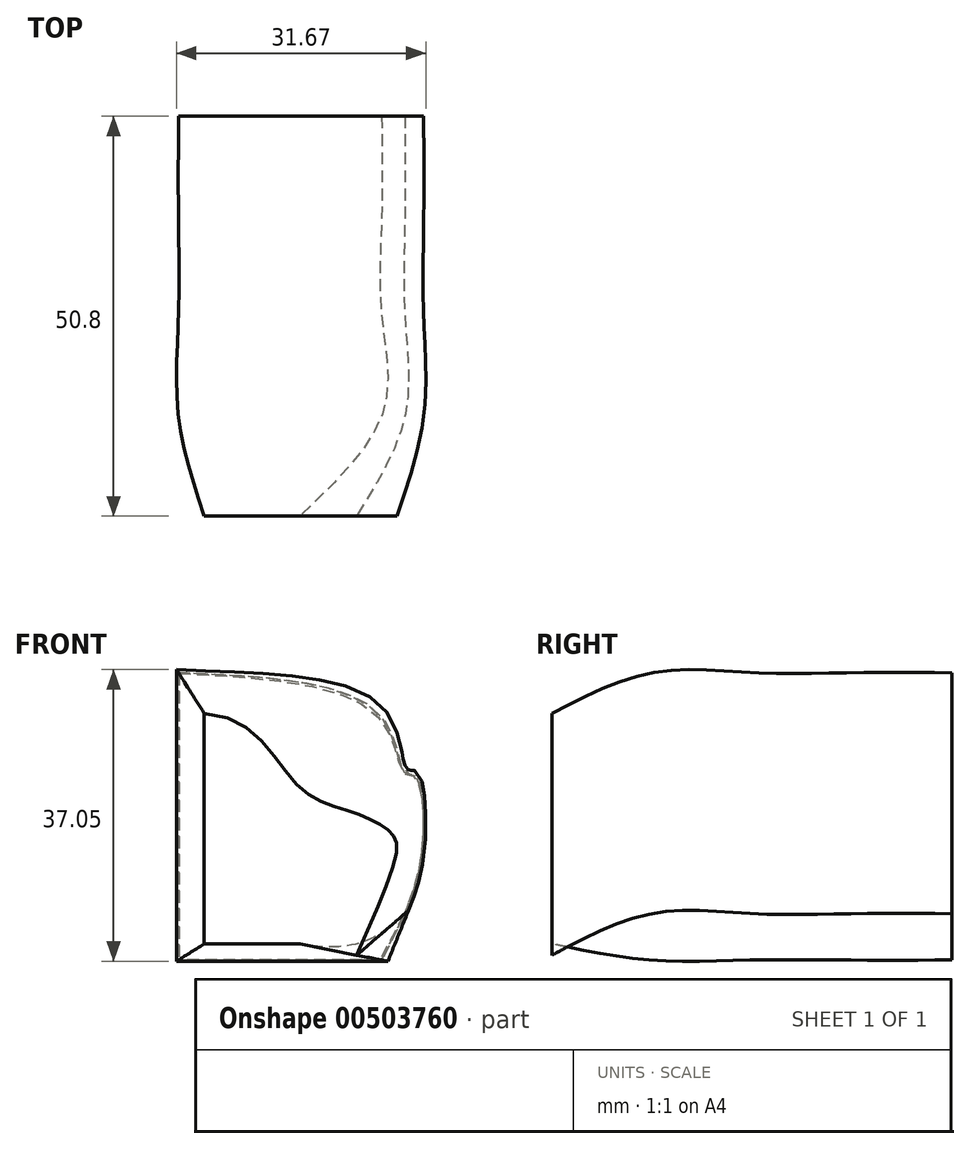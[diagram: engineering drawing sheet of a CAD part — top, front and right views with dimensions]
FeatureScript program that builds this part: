
annotation { "Feature Type Name" : "Feature", "Feature Type Description" : "" }
export const myFeature = defineFeature(function(context is Context, id is Id, definition is map)
    precondition{}
    {
        {
            var Q0;
            Q0=qCreatedBy(makeId("Front.planeOp"),FACE);
            cPlane(context, id + "F0", {"entities" : qUnion([Q0]), "cplaneType" : CPlaneType.OFFSET, "offset" : 25.4 * mm, "width" : 152.4 * mm, "height" : 152.4 * mm});
        }
        {
            var Q0;
            Q0=qCreatedBy(id+"F0.planeOp",FACE);
            cPlane(context, id + "F1", {"entities" : qUnion([Q0]), "cplaneType" : CPlaneType.OFFSET, "offset" : 12.7 * mm, "width" : 152.4 * mm, "height" : 152.4 * mm});
        }
        {
            var Q0;
            Q0=qCreatedBy(id+"F1.planeOp",FACE);
            cPlane(context, id + "F2", {"entities" : qUnion([Q0]), "cplaneType" : CPlaneType.OFFSET, "offset" : 12.7 * mm, "width" : 152.4 * mm, "height" : 152.4 * mm});
        }
        {
            var Q0;
            Q0=qCreatedBy(id+"F0.planeOp",FACE);
            cPlane(context, id + "F3", {"entities" : qUnion([Q0]), "cplaneType" : CPlaneType.OFFSET, "offset" : 12.7 * mm, "oppositeDirection" : true, "width" : 152.4 * mm, "height" : 152.4 * mm});
        }
        {
            var Q0;
            Q0=qCreatedBy(id+"F3.planeOp",FACE);
            cPlane(context, id + "F4", {"entities" : qUnion([Q0]), "cplaneType" : CPlaneType.OFFSET, "offset" : 12.7 * mm, "oppositeDirection" : true, "width" : 152.4 * mm, "height" : 152.4 * mm});
        }
        {
            var Q0;
            Q0=qCreatedBy(id+"F1.planeOp",FACE);
            var sketch = newSketch(context, id + "F5", { "sketchPlane" : qUnion([Q0])});
            skLineSegment(sketch, "E0", {"start": v(-15.42, -12) * mm, "end": v(10.4, -12) * mm});
            skLineSegment(sketch, "E1", {"start": v(10.4, -12) * mm, "end": v(13.34, -6.1) * mm});
            skFitSpline(sketch, "E2", {"points": [v(13.34, -6.1) * mm, v(15.55, 2) * mm, v(14.63, 11.4) * mm, v(13.34, 11.77) * mm, v(10.4, 18.78) * mm, v(-15.42, 24.5) * mm], "startDerivative": vector(14.36, 36.3) * mm, "endDerivative": vector(-96.3, 4.27) * mm});
            skLineSegment(sketch, "E3", {"start": v(-15.42, 24.5) * mm, "end": v(-15.42, -12) * mm});
            skSolve(sketch);
        }
        {
            var Q0;
            Q0=qCreatedBy(id+"F0.planeOp",FACE);
            var sketch = newSketch(context, id + "F6", { "sketchPlane" : qUnion([Q0])});
            skLineSegment(sketch, "E4", {"start": v(-15.42, -12) * mm, "end": v(10.4, -12) * mm});
            skLineSegment(sketch, "E5", {"start": v(10.4, -12) * mm, "end": v(13.34, -6.1) * mm});
            skFitSpline(sketch, "E6", {"points": [v(13.34, -6.1) * mm, v(15.55, 2) * mm, v(14.63, 11.4) * mm, v(13.34, 11.77) * mm, v(10.4, 18.78) * mm, v(-15.42, 24.5) * mm], "startDerivative": vector(14.36, 36.3) * mm, "endDerivative": vector(-96.3, 4.27) * mm});
            skLineSegment(sketch, "E7", {"start": v(-15.42, 24.5) * mm, "end": v(-15.42, -12) * mm});
            skSolve(sketch);
        }
        {
            var Q0;
            Q0=qCreatedBy(id+"F3.planeOp",FACE);
            var sketch = newSketch(context, id + "F7", { "sketchPlane" : qUnion([Q0])});
            skLineSegment(sketch, "E8", {"start": v(-15.42, -12) * mm, "end": v(10.4, -12) * mm});
            skLineSegment(sketch, "E9", {"start": v(10.4, -12) * mm, "end": v(13.34, -6.1) * mm});
            skFitSpline(sketch, "E10", {"points": [v(13.34, -6.1) * mm, v(15.55, 2) * mm, v(14.63, 11.4) * mm, v(13.34, 11.77) * mm, v(10.4, 18.78) * mm, v(-15.42, 24.5) * mm], "startDerivative": vector(14.36, 36.3) * mm, "endDerivative": vector(-96.3, 4.27) * mm});
            skLineSegment(sketch, "E11", {"start": v(-15.42, 24.5) * mm, "end": v(-15.42, -12) * mm});
            skSolve(sketch);
        }
        {
            var Q0;
            Q0=qCreatedBy(id+"F4.planeOp",FACE);
            var sketch = newSketch(context, id + "F8", { "sketchPlane" : qUnion([Q0])});
            skLineSegment(sketch, "E12", {"start": v(-15.42, -12) * mm, "end": v(10.4, -12) * mm});
            skLineSegment(sketch, "E13", {"start": v(10.4, -12) * mm, "end": v(13.34, -6.1) * mm});
            skFitSpline(sketch, "E14", {"points": [v(13.34, -6.1) * mm, v(15.55, 2) * mm, v(14.63, 11.4) * mm, v(13.34, 11.77) * mm, v(10.4, 18.78) * mm, v(-15.42, 24.5) * mm], "startDerivative": vector(14.36, 36.3) * mm, "endDerivative": vector(-96.3, 4.27) * mm});
            skLineSegment(sketch, "E15", {"start": v(-15.42, 24.5) * mm, "end": v(-15.42, -12) * mm});
            skSolve(sketch);
        }
        {
            var Q0;
            Q0=qCreatedBy(id+"F2.planeOp",FACE);
            var sketch = newSketch(context, id + "F9", { "sketchPlane" : qUnion([Q0])});
            skLineSegment(sketch, "E16", {"start": v(-12.15, -9.94) * mm, "end": v(0, -9.94) * mm});
            skLineSegment(sketch, "E17", {"start": v(7.21, -11.4) * mm, "end": v(0, -9.94) * mm});
            skFitSpline(sketch, "E18", {"points": [v(7.21, -11.4) * mm, v(12.25, 1.58) * mm, v(11.44, 4.28) * mm, v(7.21, 6.59) * mm, v(0, 9.91) * mm, v(-12.15, 19.3) * mm], "startDerivative": vector(11.31, 28.6) * mm, "endDerivative": vector(-75.86, 3.36) * mm});
            skLineSegment(sketch, "E19", {"start": v(-12.15, 19.3) * mm, "end": v(-12.15, -9.94) * mm});
            skSolve(sketch);
        }
        {
            var Q0;
            Q0=makeQuery(id+"F8.imprint","IMPRINT",FACE,{"disambiguationData":[TD([[makeQuery(id+"F8.imprint","IMPRINT",EDGE,{"derivedFrom":sQuery(id+"F8.wireOp",EDGE,"E12")}),1.0]])]});
            var Q1;
            Q1=makeQuery(id+"F7.imprint","IMPRINT",FACE,{"disambiguationData":[TD([[makeQuery(id+"F7.imprint","IMPRINT",EDGE,{"derivedFrom":sQuery(id+"F7.wireOp",EDGE,"E8")}),1.0]])]});
            var Q2;
            Q2=makeQuery(id+"F6.imprint","IMPRINT",FACE,{"disambiguationData":[TD([[makeQuery(id+"F6.imprint","IMPRINT",EDGE,{"derivedFrom":sQuery(id+"F6.wireOp",EDGE,"E4")}),1.0]])]});
            var Q3;
            Q3=makeQuery(id+"F5.imprint","IMPRINT",FACE,{"disambiguationData":[TD([[makeQuery(id+"F5.imprint","IMPRINT",EDGE,{"derivedFrom":sQuery(id+"F5.wireOp",EDGE,"E0")}),1.0]])]});
            var Q4;
            Q4=makeQuery(id+"F9.imprint","IMPRINT",FACE,{"disambiguationData":[TD([[makeQuery(id+"F9.imprint","IMPRINT",EDGE,{"derivedFrom":sQuery(id+"F9.wireOp",EDGE,"E16")}),1.0]])]});
            loft(context, id + "F10", {"sheetProfilesArray" : [{ "sheetProfileEntities" : qUnion([Q0]) }, { "sheetProfileEntities" : qUnion([Q1]) }, { "sheetProfileEntities" : qUnion([Q2]) }, { "sheetProfileEntities" : qUnion([Q3]) }, { "sheetProfileEntities" : qUnion([Q4]) }]});
        }
    });
